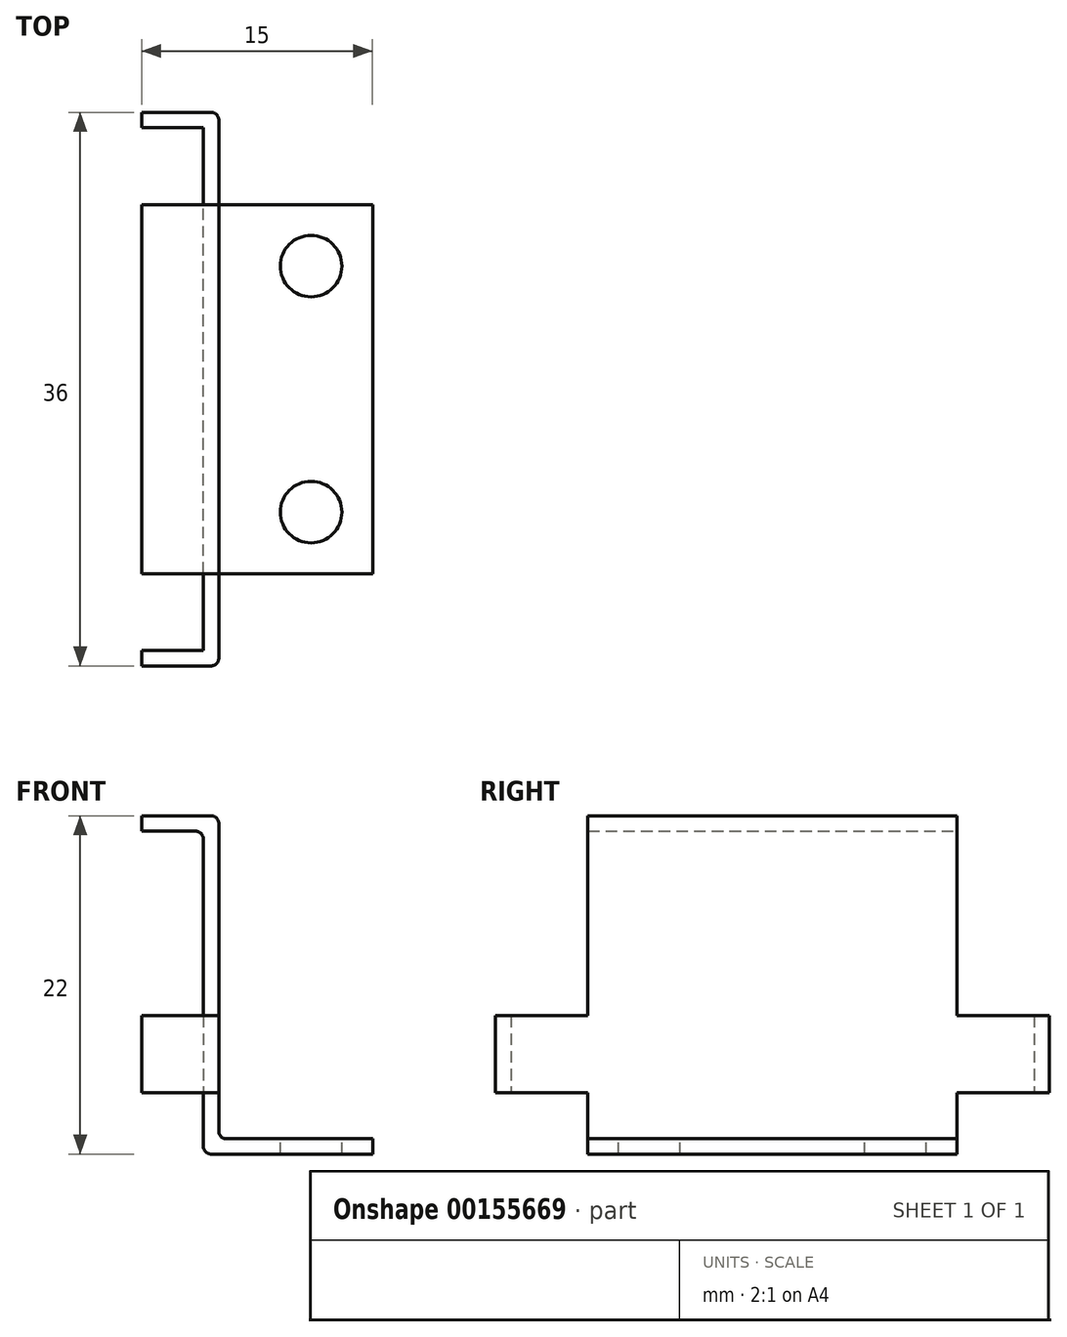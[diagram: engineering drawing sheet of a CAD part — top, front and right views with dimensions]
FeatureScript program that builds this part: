
annotation { "Feature Type Name" : "Feature", "Feature Type Description" : "" }
export const myFeature = defineFeature(function(context is Context, id is Id, definition is map)
    precondition{}
    {
        {
            var Q0;
            Q0=qCreatedBy(makeId("Front.planeOp"),FACE);
            var sketch = newSketch(context, id + "F0", { "sketchPlane" : qUnion([Q0])});
            skLineSegment(sketch, "E0.bottom", {"start": v(47.04, 40.35) * mm, "end": v(57.04, 40.35) * mm});
            skLineSegment(sketch, "E0.top", {"start": v(46.04, 39.35) * mm, "end": v(57.04, 39.35) * mm});
            skLineSegment(sketch, "E0.right", {"start": v(57.04, 40.35) * mm, "end": v(57.04, 39.35) * mm});
            skLineSegment(sketch, "E1.left", {"start": v(47.04, 40.35) * mm, "end": v(47.04, 61.35) * mm});
            skLineSegment(sketch, "E1.right", {"start": v(46.04, 39.35) * mm, "end": v(46.04, 60.35) * mm});
            skLineSegment(sketch, "E2.bottom", {"start": v(46.04, 60.35) * mm, "end": v(42.04, 60.35) * mm});
            skLineSegment(sketch, "E2.top", {"start": v(47.04, 61.35) * mm, "end": v(42.04, 61.35) * mm});
            skLineSegment(sketch, "E2.right", {"start": v(42.04, 60.35) * mm, "end": v(42.04, 61.35) * mm});
            skSolve(sketch);
        }
        {
            var Q0;
            Q0=qSketchRegion(id+"F0",true);
            extrude(context, id + "F1", {"entities" : qUnion([Q0]), "depth" : 24 * mm});
        }
        {
            var Q0;
            Q0=makeQuery(id+"F1.opExtrude","SWEPT_FACE",FACE,{"disambiguationData":[OSD([sQuery(id+"F0.wireOp",EDGE,"E0.bottom")])]});
            var sketch = newSketch(context, id + "F2", { "sketchPlane" : qUnion([Q0])});
            skPoint(sketch, "E3.middle", {"position": v(53.04, -20) * mm});
            skPoint(sketch, "E4.middle", {"position": v(53.04, -4) * mm});
            skCircle(sketch, "E5", {"center": v(53.04, -20) * mm, "radius": 2 * mm});
            skCircle(sketch, "E6", {"center": v(53.04, -4) * mm, "radius": 2 * mm});
            skSolve(sketch);
        }
        {
            var Q0;
            Q0=qSketchRegion(id+"F2",true);
            extrude(context, id + "F3", {"entities" : qUnion([Q0]), "operationType" : NewBodyOperationType.REMOVE, "oppositeDirection" : true, "depth" : 2 * mm});
        }
        {
            var Q0;
            Q0=makeQuery(id+"F1.opExtrude","SWEPT_FACE",FACE,{"disambiguationData":[OSD([sQuery(id+"F0.wireOp",EDGE,"E1.left")])]});
            var sketch = newSketch(context, id + "F4", { "sketchPlane" : qUnion([Q0])});
            skLineSegment(sketch, "E7.bottom", {"start": v(-24, 48.35) * mm, "end": v(-30, 48.35) * mm});
            skLineSegment(sketch, "E7.top", {"start": v(-24, 43.35) * mm, "end": v(-30, 43.35) * mm});
            skLineSegment(sketch, "E7.left", {"start": v(-24, 48.35) * mm, "end": v(-24, 43.35) * mm});
            skLineSegment(sketch, "E7.right", {"start": v(-30, 48.35) * mm, "end": v(-30, 43.35) * mm});
            skLineSegment(sketch, "E8.bottom", {"start": v(0, 48.35) * mm, "end": v(6, 48.35) * mm});
            skLineSegment(sketch, "E8.top", {"start": v(0, 43.35) * mm, "end": v(6, 43.35) * mm});
            skLineSegment(sketch, "E8.left", {"start": v(0, 48.35) * mm, "end": v(0, 43.35) * mm});
            skLineSegment(sketch, "E8.right", {"start": v(6, 48.35) * mm, "end": v(6, 43.35) * mm});
            skSolve(sketch);
        }
        {
            var Q0;
            Q0 = qSketchRegion(id + "F4", true);
            extrude(context, id + "F5", {"entities" : qUnion([Q0]), "operationType" : NewBodyOperationType.ADD, "oppositeDirection" : true, "depth" : 1 * mm});
        }
        {
            var Q0;
            Q0=makeQuery(id+"F5.boolean.opBoolean","MERGE",FACE,{"derivedFrom":[makeQuery(id+"F1.opExtrude","SWEPT_FACE",FACE,{"disambiguationData":[OSD([sQuery(id+"F0.wireOp",EDGE,"E1.right")])]}),makeQuery(id+"F5.opExtrude","CAP_FACE",FACE,{"disambiguationData":[OSD([sQuery(id+"F4.wireOp",EDGE,"E7.bottom"),sQuery(id+"F4.wireOp",EDGE,"E7.top"),sQuery(id+"F4.wireOp",EDGE,"E7.left"),sQuery(id+"F4.wireOp",EDGE,"E7.right")])],"isStart":false}),makeQuery(id+"F5.opExtrude","CAP_FACE",FACE,{"disambiguationData":[OSD([sQuery(id+"F4.wireOp",EDGE,"E8.bottom"),sQuery(id+"F4.wireOp",EDGE,"E8.top"),sQuery(id+"F4.wireOp",EDGE,"E8.left"),sQuery(id+"F4.wireOp",EDGE,"E8.right")])],"isStart":false})]});
            var sketch = newSketch(context, id + "F6", { "sketchPlane" : qUnion([Q0])});
            skLineSegment(sketch, "E9.bottom", {"start": v(-6, 48.35) * mm, "end": v(-5, 48.35) * mm});
            skLineSegment(sketch, "E9.top", {"start": v(-6, 43.35) * mm, "end": v(-5, 43.35) * mm});
            skLineSegment(sketch, "E9.left", {"start": v(-6, 48.35) * mm, "end": v(-6, 43.35) * mm});
            skLineSegment(sketch, "E9.right", {"start": v(-5, 48.35) * mm, "end": v(-5, 43.35) * mm});
            skLineSegment(sketch, "E10.bottom", {"start": v(30, 48.35) * mm, "end": v(29, 48.35) * mm});
            skLineSegment(sketch, "E10.top", {"start": v(30, 43.35) * mm, "end": v(29, 43.35) * mm});
            skLineSegment(sketch, "E10.left", {"start": v(30, 48.35) * mm, "end": v(30, 43.35) * mm});
            skLineSegment(sketch, "E10.right", {"start": v(29, 48.35) * mm, "end": v(29, 43.35) * mm});
            skSolve(sketch);
        }
        {
            var Q0;
            Q0 = qSketchRegion(id + "F6", true);
            extrude(context, id + "F7", {"entities" : qUnion([Q0]), "operationType" : NewBodyOperationType.ADD, "depth" : 4 * mm});
        }
        {
            var Q0;
            Q0=makeQuery(id+"F1.opExtrude","SWEPT_EDGE",EDGE,{"disambiguationData":[OSD([sQuery(id+"F0.wireOp",EDGE,"E0.bottom"),sQuery(id+"F0.wireOp",EDGE,"E1.left")])]});
            var Q1;
            Q1=makeQuery(id+"F1.opExtrude","SWEPT_EDGE",EDGE,{"disambiguationData":[OSD([sQuery(id+"F0.wireOp",EDGE,"E0.top"),sQuery(id+"F0.wireOp",EDGE,"E1.right")])]});
            var Q2;
            Q2=makeQuery(id+"F1.opExtrude","SWEPT_EDGE",EDGE,{"disambiguationData":[OSD([sQuery(id+"F0.wireOp",EDGE,"E1.left"),sQuery(id+"F0.wireOp",EDGE,"E2.top")])]});
            var Q3;
            Q3=makeQuery(id+"F1.opExtrude","SWEPT_EDGE",EDGE,{"disambiguationData":[OSD([sQuery(id+"F0.wireOp",EDGE,"E1.right"),sQuery(id+"F0.wireOp",EDGE,"E2.bottom")])]});
            var Q4;
            Q4=makeQuery(id+"F5.opExtrude","CAP_EDGE",EDGE,{"disambiguationData":[OSD([sQuery(id+"F4.wireOp",EDGE,"E7.right")])],"isStart":true});
            var Q5;
            Q5=makeQuery(id+"F7.opExtrude","CAP_EDGE",EDGE,{"disambiguationData":[OSD([sQuery(id+"F6.wireOp",EDGE,"E10.right")])],"isStart":true});
            var Q6;
            Q6=makeQuery(id+"F7.opExtrude","CAP_EDGE",EDGE,{"disambiguationData":[OSD([sQuery(id+"F6.wireOp",EDGE,"E9.right")])],"isStart":true});
            var Q7;
            Q7=makeQuery(id+"F5.opExtrude","CAP_EDGE",EDGE,{"disambiguationData":[OSD([sQuery(id+"F4.wireOp",EDGE,"E8.right")])],"isStart":true});
            fillet(context, id + "F8", {"entities" : qUnion([Q0, Q1, Q2, Q3, Q4, Q5, Q6, Q7]), "radius" : 0.5 * mm, "tangentPropagation" : true, "allowEdgeOverflow" : false});
        }
    });
